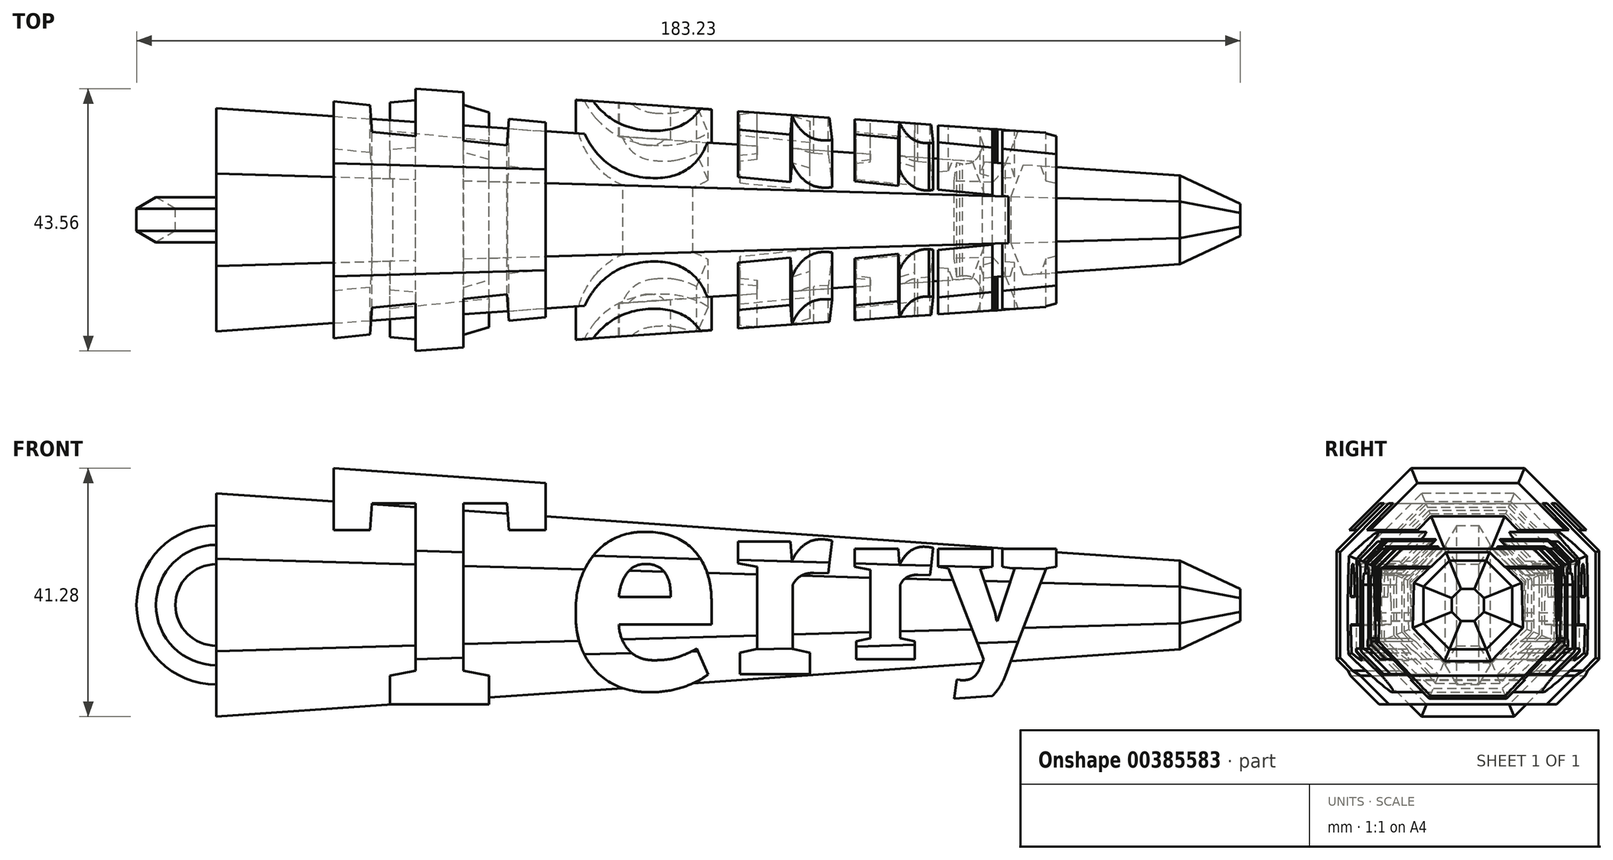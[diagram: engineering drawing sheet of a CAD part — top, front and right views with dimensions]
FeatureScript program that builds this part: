
annotation { "Feature Type Name" : "Feature", "Feature Type Description" : "" }
export const myFeature = defineFeature(function(context is Context, id is Id, definition is map)
    precondition{}
    {
        {
            assignVariable(context, id + "F0", {"name" : "hookPlane", "anyValue" : 80});
        }
        {
            assignVariable(context, id + "F1", {"name" : "halfLength", "anyValue" : 80});
        }
        {
            var Q0;
            Q0=qCreatedBy(makeId("Front.planeOp"),FACE);
            var sketch = newSketch(context, id + "F2", { "sketchPlane" : qUnion([Q0])});
            skText(sketch, "E0", { "text": "T", "fontName": "RobotoSlab-Bold.ttf"});
            skPoint(sketch, "E1", {"position": v(-21.9, 0) * mm});
            skText(sketch, "E2", { "text": "e", "fontName": "RobotoSlab-Bold.ttf"});
            skText(sketch, "E3", { "text": "r", "fontName": "RobotoSlab-Bold.ttf"});
            skText(sketch, "E4", { "text": "ry", "fontName": "RobotoSlab-Bold.ttf"});
            skPoint(sketch, "E5", {"position": v(5.2, 0) * mm});
            skPoint(sketch, "E6", {"position": v(24.8, 0) * mm});
            skLineSegment(sketch, "E7", {"start": v(-61.6, -20) * mm, "end": v(-61.6, -51.65) * mm, "construction": true});
            skLineSegment(sketch, "E8", {"start": v(-61.6, -51.65) * mm, "end": v(61.6, -51.65) * mm, "construction": true});
            skLineSegment(sketch, "E9", {"start": v(61.6, -51.65) * mm, "end": v(61.6, -12.5) * mm, "construction": true});
            skPoint(sketch, "E10", {"position": v(0, -51.65) * mm});
            const initialGuessF2  = {"E0": [-0.0616, -0.02, 1, 0, 0.04], "E2": [-0.0219, -0.0175, 1, 0, 0.035], "E3": [0.0052, -0.015, 1, 0, 0.03], "E4": [0.0248, -0.0125, 1, 0, 0.025]};
            skSetInitialGuess(sketch, initialGuessF2);
            skSolve(sketch);
        }
        {
            var Q0;
            Q0=qSketchRegion(id+"F2",true);
            extrude(context, id + "F3", {"entities" : qUnion([Q0]), "depth" : 25 * mm, "hasSecondDirection" : true, "secondDirectionOppositeDirection" : true, "secondDirectionDepth" : 25 * mm});
        }
        {
            var Q0;
            Q0=qCreatedBy(makeId("Right.planeOp"),FACE);
            var sketch = newSketch(context, id + "F4", { "sketchPlane" : qUnion([Q0])});
            skCircle(sketch, "E11", {"center": v(0, -3.5) * mm, "radius": 12.5 * mm, "construction": true});
            skCircle(sketch, "E12.cCircle", {"center": v(0, -3.5) * mm, "radius": 12.95 * mm, "construction": true});
            skLineSegment(sketch, "E12.0", {"start": v(-5.36, 9.44) * mm, "end": v(5.36, 9.44) * mm});
            skLineSegment(sketch, "E12.1", {"start": v(5.36, 9.44) * mm, "end": v(12.95, 1.86) * mm});
            skLineSegment(sketch, "E12.2", {"start": v(12.95, 1.86) * mm, "end": v(12.95, -8.87) * mm});
            skLineSegment(sketch, "E12.3", {"start": v(12.95, -8.87) * mm, "end": v(5.36, -16.45) * mm});
            skLineSegment(sketch, "E12.4", {"start": v(5.36, -16.45) * mm, "end": v(-5.36, -16.45) * mm});
            skLineSegment(sketch, "E12.5", {"start": v(-5.36, -16.45) * mm, "end": v(-12.95, -8.87) * mm});
            skLineSegment(sketch, "E12.6", {"start": v(-12.95, -8.87) * mm, "end": v(-12.95, 1.86) * mm});
            skLineSegment(sketch, "E12.7", {"start": v(-12.95, 1.86) * mm, "end": v(-5.36, 9.44) * mm});
            skPoint(sketch, "E12.0.midPoint", {"position": v(0, 9.44) * mm});
            skLineSegment(sketch, "E13", {"start": v(0, 19.5) * mm, "end": v(0, 9.44) * mm, "construction": true});
            skSolve(sketch);
        }
        {
            var Q0;
            Q0=qSketchRegion(id+"F4",true);
            var Q1;
            Q1=makeQuery(id+"F3.opExtrude","SWEPT_FACE",FACE,{"disambiguationData":[OSD([sQuery(id+"F2.wireOp",EDGE,"E4.sketch_text.stroke-1")])]});
            extrude(context, id + "F5", {"entities" : qUnion([Q0]), "operationType" : NewBodyOperationType.ADD, "oppositeDirection" : true, "depth" : (getVariable(context, 'halfLength')) * mm, "hasDraft" : true, "draftAngle" : 4 * degree, "hasSecondDirection" : true, "secondDirectionOppositeDirection" : false, "secondDirectionBoundEntityFace" : qUnion([Q1]), "secondDirectionDepth" : (getVariable(context, 'halfLength')) * mm, "hasSecondDirectionDraft" : true, "secondDirectionDraftAngle" : 4 * degree, "secondDirectionDraftPullDirection" : true});
        }
        {
            var Q0;
            Q0=qCreatedBy(makeId("Right.planeOp"),FACE);
            var sketch = newSketch(context, id + "F6", { "sketchPlane" : qUnion([Q0])});
            skCircle(sketch, "E14.cCircle", {"center": v(0, -3.5) * mm, "radius": 18.5 * mm, "construction": true});
            skLineSegment(sketch, "E14.0", {"start": v(-7.66, 15) * mm, "end": v(7.66, 15) * mm});
            skLineSegment(sketch, "E14.1", {"start": v(7.66, 15) * mm, "end": v(18.5, 4.16) * mm});
            skLineSegment(sketch, "E14.2", {"start": v(18.5, 4.16) * mm, "end": v(18.5, -11.17) * mm});
            skLineSegment(sketch, "E14.3", {"start": v(18.5, -11.17) * mm, "end": v(7.66, -22) * mm});
            skLineSegment(sketch, "E14.4", {"start": v(7.66, -22) * mm, "end": v(-7.66, -22) * mm});
            skLineSegment(sketch, "E14.5", {"start": v(-7.66, -22) * mm, "end": v(-18.5, -11.17) * mm});
            skLineSegment(sketch, "E14.6", {"start": v(-18.5, -11.17) * mm, "end": v(-18.5, 4.16) * mm});
            skLineSegment(sketch, "E14.7", {"start": v(-18.5, 4.16) * mm, "end": v(-7.66, 15) * mm});
            skLineSegment(sketch, "E15.bottom", {"start": v(37.5, 34) * mm, "end": v(-37.5, 34) * mm});
            skLineSegment(sketch, "E15.top", {"start": v(37.5, -41) * mm, "end": v(-37.5, -41) * mm});
            skLineSegment(sketch, "E15.left", {"start": v(37.5, 34) * mm, "end": v(37.5, -41) * mm});
            skLineSegment(sketch, "E15.right", {"start": v(-37.5, 34) * mm, "end": v(-37.5, -41) * mm});
            skLineSegment(sketch, "E16", {"start": v(0, 19.5) * mm, "end": v(0, -8.52) * mm, "construction": true});
            skSolve(sketch);
        }
        {
            var Q0;
            Q0=makeQuery(id+"F6.imprint","IMPRINT",FACE,{"disambiguationData":[TD([[makeQuery(id+"F6.imprint","IMPRINT",EDGE,{"derivedFrom":sQuery(id+"F6.wireOp",EDGE,"E14.0")}),1.0]])]});
            extrude(context, id + "F7", {"entities" : qUnion([Q0]), "operationType" : NewBodyOperationType.REMOVE, "endBound" : BoundingType.THROUGH_ALL, "depth" : 25 * mm, "hasDraft" : true, "draftAngle" : 4 * degree, "hasSecondDirection" : true, "secondDirectionBound" : SecondDirectionBoundingType.THROUGH_ALL, "secondDirectionOppositeDirection" : true, "secondDirectionDepth" : 25 * mm, "hasSecondDirectionDraft" : true, "secondDirectionDraftAngle" : 4 * degree, "secondDirectionDraftPullDirection" : true});
        }
        {
            var Q0;
            {var subQ0=sQuery(id+"F4.wireOp",EDGE,"E12.3");var subQ1=sQuery(id+"F4.wireOp",EDGE,"E12.2");var subQ2=sQuery(id+"F4.wireOp",EDGE,"E12.4");var subQ3=sQuery(id+"F4.wireOp",EDGE,"E12.5");var subQ4=sQuery(id+"F4.wireOp",EDGE,"E12.6");Q0=makeQuery(id+"F5.boolean.opBoolean","SPLIT",FACE,{"disambiguationData":[TD([makeQuery(id+"F3.opExtrude","SWEPT_FACE",FACE,{"disambiguationData":[OSD([sQuery(id+"F2.wireOp",EDGE,"E4.sketch_text.stroke-0")])]})])],"derivedFrom":makeQuery(id+"F5.opExtrude","CAP_FACE",FACE,{"disambiguationData":[OSD([sQuery(id+"F4.wireOp",EDGE,"E12.0"),sQuery(id+"F4.wireOp",EDGE,"E12.1"),subQ1,subQ0,subQ2,subQ3,subQ4,sQuery(id+"F4.wireOp",EDGE,"E12.7")])],"isStart":true})});}
            var sketch = newSketch(context, id + "F8", { "sketchPlane" : qUnion([Q0])});
            skCircle(sketch, "E17.cCircle", {"center": v(0, -3.5) * mm, "radius": 7.35 * mm, "construction": true});
            skLineSegment(sketch, "E17.0", {"start": v(-3.05, 3.85) * mm, "end": v(3.05, 3.85) * mm});
            skLineSegment(sketch, "E17.1", {"start": v(3.05, 3.85) * mm, "end": v(7.35, -0.46) * mm});
            skLineSegment(sketch, "E17.2", {"start": v(7.35, -0.46) * mm, "end": v(7.35, -6.55) * mm});
            skLineSegment(sketch, "E17.3", {"start": v(7.35, -6.55) * mm, "end": v(3.05, -10.86) * mm});
            skLineSegment(sketch, "E17.4", {"start": v(3.05, -10.86) * mm, "end": v(-3.05, -10.86) * mm});
            skLineSegment(sketch, "E17.5", {"start": v(-3.05, -10.86) * mm, "end": v(-7.35, -6.55) * mm});
            skLineSegment(sketch, "E17.6", {"start": v(-7.35, -6.55) * mm, "end": v(-7.35, -0.46) * mm});
            skLineSegment(sketch, "E17.7", {"start": v(-7.35, -0.46) * mm, "end": v(-3.05, 3.85) * mm});
            skPoint(sketch, "E17.0.midPoint", {"position": v(0, 3.85) * mm});
            skLineSegment(sketch, "E18", {"start": v(0, 19.59) * mm, "end": v(0, -20.57) * mm, "construction": true});
            skSolve(sketch);
        }
        {
            var Q0;
            Q0=qSketchRegion(id+"F8",true);
            extrude(context, id + "F9", {"entities" : qUnion([Q0]), "operationType" : NewBodyOperationType.ADD, "depth" : 10 * mm, "hasDraft" : true, "draftAngle" : 25 * degree, "draftPullDirection" : true});
        }
        {
            var Q0;
            Q0=qCreatedBy(makeId("Right.planeOp"),FACE);
            cPlane(context, id + "F10", {"entities" : qUnion([Q0]), "cplaneType" : CPlaneType.OFFSET, "offset" : (getVariable(context, 'hookPlane')) * mm, "oppositeDirection" : true, "width" : 150 * mm, "height" : 150 * mm});
        }
        {
            var Q0;
            Q0=qCreatedBy(makeId("Front.planeOp"),FACE);
            var sketch = newSketch(context, id + "F11", { "sketchPlane" : qUnion([Q0])});
            skArc(sketch, "E19", {"start": v(-73.39, 4) * mm, "mid": v(-90, -3.5) * mm, "end": v(-73.39, -11) * mm});
            skLineSegment(sketch, "E20", {"start": v(-73.39, 4) * mm, "end": v(-73.39, -11) * mm, "construction": true});
            skPoint(sketch, "E21", {"position": v(-73.39, -3.5) * mm});
            skLineSegment(sketch, "E22", {"start": v(-80, 15.04) * mm, "end": v(-80, -22.05) * mm, "construction": true});
            skSolve(sketch);
        }
        {
            var Q0;
            Q0=qCreatedBy(id+"F10.planeOp",FACE);
            var sketch = newSketch(context, id + "F12", { "sketchPlane" : qUnion([Q0])});
            skCircle(sketch, "E23.cCircle", {"center": v(0, 6.5) * mm, "radius": 3.23 * mm, "construction": true});
            skLineSegment(sketch, "E23.0", {"start": v(1.87, 3.26) * mm, "end": v(-1.87, 3.26) * mm});
            skLineSegment(sketch, "E23.1", {"start": v(-1.87, 3.26) * mm, "end": v(-3.73, 6.5) * mm});
            skLineSegment(sketch, "E23.2", {"start": v(-3.73, 6.5) * mm, "end": v(-1.87, 9.73) * mm});
            skLineSegment(sketch, "E23.3", {"start": v(-1.87, 9.73) * mm, "end": v(1.87, 9.73) * mm});
            skLineSegment(sketch, "E23.4", {"start": v(1.87, 9.73) * mm, "end": v(3.73, 6.5) * mm});
            skLineSegment(sketch, "E23.5", {"start": v(3.73, 6.5) * mm, "end": v(1.87, 3.26) * mm});
            skPoint(sketch, "E23.0.midPoint", {"position": v(0, 3.26) * mm});
            skSolve(sketch);
        }
        {
            var Q0;
            Q0=qSketchRegion(id+"F12",true);
            var Q1;
            Q1=qConstructionFilter(qBodyType(qCreatedBy(id+"F11",EDGE),BodyType.WIRE),ConstructionObject.NO);
            sweep(context, id + "F13", {"operationType" : NewBodyOperationType.ADD, "profiles" : qUnion([Q0]), "path" : qUnion([Q1])});
        }
    });
